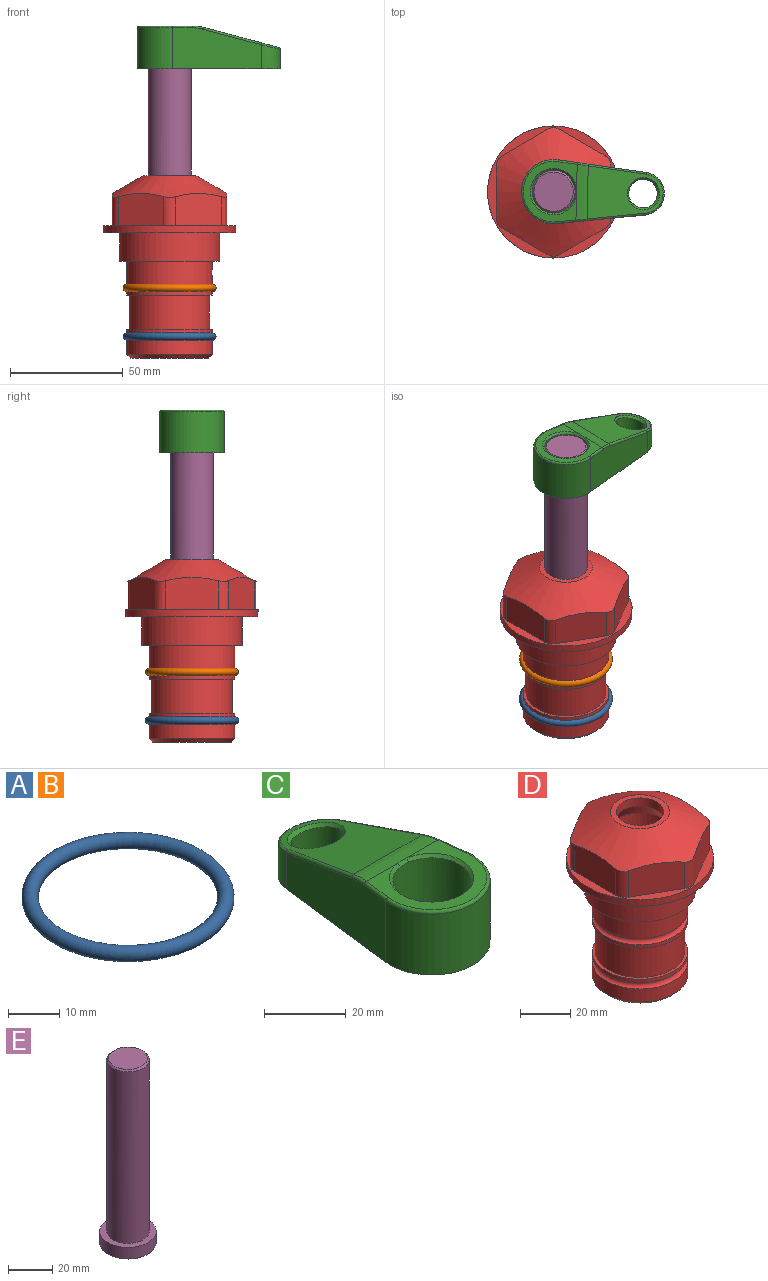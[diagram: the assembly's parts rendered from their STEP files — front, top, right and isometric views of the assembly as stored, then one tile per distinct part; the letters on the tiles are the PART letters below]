
ASSEMBLY  parts=5 mates=4
PART A: 1 faces, bbox 44.7x44.7x3.2 mm
  f0: torus R=19.05mm, axis (0,0,1), area 1193.9mm2
PART B: same geometry as A
PART C: 31 faces, bbox 31.7x65.5x19.8 mm
  f0: plane 39.12x18.26mm, normal (0.99,0.12,0), area 612.2mm2, adj f1,f4,f7,f11,f13,f15
  f1: cylinder r=9.53mm len=18.91mm, axis (0,0,-1), area 296.1mm2, adj f0,f2,f7,f17
  f2: plane 39.12x18.26mm, normal (-0.99,0.12,0), area 612.2mm2, adj f1,f4,f7,f12,f14,f16
  f3: cylinder r=6.35mm len=12.7mm, axis (0,0,-1), area 362.4mm2, adj f7,f18
  f4: cylinder r=14.29mm len=28.58mm, axis (0,0,-1), area 882.2mm2, adj f0,f2,f7,f10
  f5: cylinder r=9.53mm len=19.05mm, axis (0,0,-1), area 1092.6mm2, adj f7,f19,f20
  f6: plane 26.99x23.69mm, normal (0,0,1), area 216.2mm2, adj f9,f10,f11,f12,f19
  f7: plane 63.5x28.58mm, normal (0,0,-1), area 661.8mm2, adj f0,f1,f2,f3,f4,f5,f22,f23
  f8: plane 33.52x23.6mm, normal (0,0.26,0.97), area 486mm2, adj f9,f15,f16,f17,f18
  f9: cylinder r=19.05mm len=24.72mm, axis (1,0,0), area 120.4mm2, adj f6,f8,f13,f14,f20
  f10: torus R=13.49mm, axis (0,0,1), area 59mm2, adj f4,f6,f11,f12
  f11: cylinder r=0.79mm len=8.67mm, axis (0.12,-0.99,0), area 10.8mm2, adj f0,f6,f10,f13
  f12: cylinder r=0.79mm len=8.67mm, axis (0.12,0.99,0), area 10.8mm2, adj f2,f6,f10,f14
  f13: bspline ~4.95x1.42mm, area 6.1mm2, adj f0,f9,f11,f15
  f14: bspline ~4.95x1.42mm, area 6.1mm2, adj f2,f9,f12,f16
  f15: cylinder r=0.79mm len=25.95mm, axis (0.12,-0.96,0.26), area 32.9mm2, adj f0,f8,f13,f17
  f16: cylinder r=0.79mm len=25.95mm, axis (0.12,0.96,-0.26), area 32.9mm2, adj f2,f8,f14,f17
  f17: bspline ~18.91x8.38mm, area 30mm2, adj f1,f8,f15,f16
  f18: bspline ~14.29x14.29mm, area 48.3mm2, adj f3,f8
  f19: cone r=9.53mm half-angle=45deg, axis (0,0,1), area 66.5mm2, adj f5,f6,f20
  f20: bspline ~3.22x0.96mm, area 3.5mm2, adj f5,f9,f19
  f21: plane 2.75x2.72mm, normal (0,0,-1), area 2.9mm2, adj f23,f25,f28
  f22: plane 23.05x15.88mm, normal (-0.99,-0.12,0), area 323.6mm2, adj f7,f25,f26,f27,f28,f29
  f23: plane 23.05x15.88mm, normal (0.99,-0.12,0), area 323.6mm2, adj f7,f21,f25,f27,f28,f30
  f24: cylinder r=9.53mm len=10.69mm, axis (0,0,-1), area 114.7mm2, adj f7,f27,f29,f30
  f25: cylinder r=12.7mm len=20.59mm, axis (0,0,-1), area 381.1mm2, adj f7,f21,f22,f23,f26,f28
  f26: plane 2.75x2.72mm, normal (0,0,-1), area 2.9mm2, adj f22,f25,f28
  f27: plane 19.72x18.37mm, normal (0,-0.26,-0.97), area 291.8mm2, adj f22,f23,f24,f28,f29,f30
  f28: cylinder r=15.88mm len=19.92mm, axis (1,0,0), area 54.8mm2, adj f21,f22,f23,f25,f26,f27
  f29: cylinder r=1.59mm len=11mm, axis (0,0,-1), area 34.7mm2, adj f7,f22,f24,f27
  f30: cylinder r=1.59mm len=11mm, axis (0,0,-1), area 34.7mm2, adj f7,f23,f24,f27
PART D: 36 faces, bbox 58.7x58.7x81 mm
  f0: cylinder r=17.78mm len=35.56mm, axis (0,0,1), area 1670.8mm2, adj f23,f24,f31
  f1: cylinder r=19.05mm len=38.1mm, axis (0,0,1), area 1191.9mm2, adj f26,f27,f30
  f2: plane 58.66x58.66mm, normal (0,0,-1), area 1150.6mm2, adj f3,f28
  f3: cylinder r=29.33mm len=58.66mm, axis (0,0,-1), area 585.1mm2, adj f2,f4
  f4: plane 58.66x58.66mm, normal (0,0,1), area 475.9mm2, adj f3,f5,f6,f7,f8,f9,f10,f11
  f5: plane 20.32x14.34mm, normal (-0.5,0.87,0), area 324.4mm2, adj f4,f15,f16,f17
  f6: plane 20.32x14.34mm, normal (0.5,0.87,0), area 324.4mm2, adj f4,f14,f15,f17
  f7: plane 23.48x14.34mm, normal (1,0,0), area 324.4mm2, adj f4,f13,f14,f17
  f8: plane 20.32x14.34mm, normal (0.5,-0.87,0), area 324.4mm2, adj f4,f12,f13,f17
  f9: plane 20.32x14.34mm, normal (-0.5,-0.87,0), area 324.4mm2, adj f4,f11,f12,f17
  f10: plane 23.48x14.34mm, normal (-1,0,0), area 324.4mm2, adj f4,f11,f16,f17
  f11: cylinder r=5.08mm len=12.85mm, axis (0,0,-1), area 67.2mm2, adj f4,f9,f10,f17
  f12: cylinder r=5.08mm len=12.85mm, axis (0,0,-1), area 67.2mm2, adj f4,f8,f9,f17
  f13: cylinder r=5.08mm len=12.85mm, axis (0,0,-1), area 67.2mm2, adj f4,f7,f8,f17
  f14: cylinder r=5.08mm len=12.85mm, axis (0,0,-1), area 67.2mm2, adj f4,f6,f7,f17
  f15: cylinder r=5.08mm len=12.85mm, axis (0,0,-1), area 67.2mm2, adj f4,f5,f6,f17
  f16: cylinder r=5.08mm len=12.85mm, axis (0,0,-1), area 67.2mm2, adj f4,f5,f10,f17
  f17: cone r=11.73mm half-angle=60deg, axis (0,0,-1), area 2071.8mm2, adj f5,f6,f7,f8,f9,f10,f11,f12
  f18: plane 23.46x23.46mm, normal (0,0,1), area 147.4mm2, adj f17,f35
  f19: plane 34.93x34.93mm, normal (0,0,-1), area 958mm2, adj f29
  f20: cylinder r=19.05mm len=38.1mm, axis (0,0,1), area 760.1mm2, adj f21,f29
  f21: torus R=19.05mm, axis (0,0,1), area 565.3mm2, adj f20,f22
  f22: cylinder r=19.05mm len=38.1mm, axis (0,0,1), area 190mm2, adj f21,f23
  f23: plane 38.1x38.1mm, normal (0,0,1), area 146.9mm2, adj f0,f22
  f24: plane 38.1x38.1mm, normal (0,0,-1), area 146.9mm2, adj f0,f25
  f25: cylinder r=19.05mm len=38.1mm, axis (0,0,1), area 190mm2, adj f24,f26
  f26: torus R=19.05mm, axis (0,0,1), area 565.3mm2, adj f1,f25
  f27: plane 44.45x44.45mm, normal (0,0,-1), area 411.7mm2, adj f1,f28
  f28: cylinder r=22.23mm len=44.45mm, axis (0,0,1), area 1773.5mm2, adj f2,f27
  f29: cone r=19.05mm half-angle=45deg, axis (0,0,1), area 257.5mm2, adj f19,f20
  f30: cylinder r=3.17mm len=6.75mm, axis (-1,0,0), area 128mm2, adj f1,f33
  f31: cylinder r=3.17mm len=6.35mm, axis (-1,0,0), area 102.5mm2, adj f0,f33
  f32: plane 25.4x25.4mm, normal (0,0,1), area 506.7mm2, adj f33
  f33: cylinder r=12.7mm len=66.42mm, axis (0,0,-1), area 5236.2mm2, adj f30,f31,f32,f34
  f34: cone r=9.53mm half-angle=30deg, axis (0,0,-1), area 443.4mm2, adj f33,f35
  f35: cylinder r=9.53mm len=19.05mm, axis (0,0,-1), area 240.9mm2, adj f18,f34
PART E: 6 faces, bbox 25.4x25.4x101.6 mm
  f0: plane 17.46x17.46mm, normal (0,0,1), area 239.5mm2, adj f5
  f1: plane 25.4x25.4mm, normal (0,0,-1), area 506.7mm2, adj f2
  f2: cylinder r=12.7mm len=25.4mm, axis (0,0,1), area 506.7mm2, adj f1,f3
  f3: plane 25.4x25.4mm, normal (0,0,1), area 221.7mm2, adj f2,f4
  f4: cylinder r=9.53mm len=94.46mm, axis (0,0,1), area 5653mm2, adj f3,f5
  f5: cone r=8.73mm half-angle=45deg, axis (0,0,-1), area 64.4mm2, adj f0,f4
PLACE A t=(0,0,-21.59)mm
PLACE B at identity
PLACE C rot(axis=(0,0,-1),91.3deg) t=(0,0,28.35)mm
PLACE D at identity fixed
PLACE E rot(axis=(0,0,-1),91.3deg) t=(0,0,27.55)mm
MATE fastened D.f0 <-> B.f0  axis (0,0,1) through (0,0,-24.51)mm
MATE fastened D.f0 <-> A.f0  axis (0,0,1) through (0,0,-46.1)mm
MATE fastened E.f2 <-> C.f4  axis (0,0,1) through (0,0,91.05)mm
MATE cylindrical E.f2 <-> D.f0  axis (0,0,-1) through (0,0,-10.55)mm
